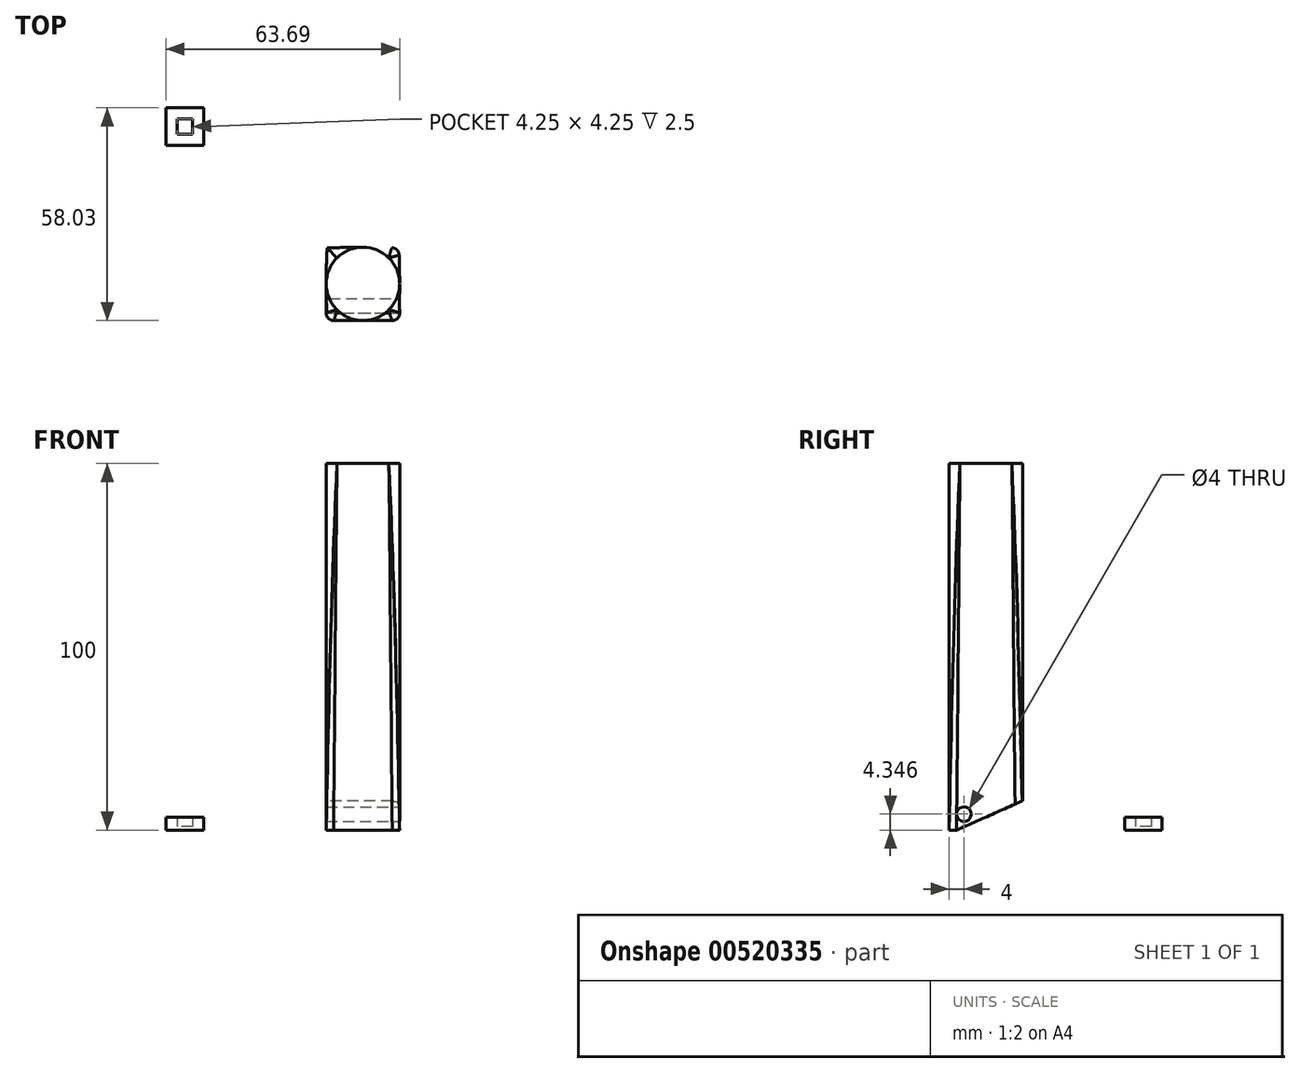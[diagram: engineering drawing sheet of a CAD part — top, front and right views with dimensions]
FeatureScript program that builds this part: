
annotation { "Feature Type Name" : "Feature", "Feature Type Description" : "" }
export const myFeature = defineFeature(function(context is Context, id is Id, definition is map)
    precondition{}
    {
        {
            var Q0;
            Q0=qCreatedBy(makeId("Top.planeOp"),FACE);
            var sketch = newSketch(context, id + "F0", { "sketchPlane" : qUnion([Q0])});
            skLineSegment(sketch, "E0.bottom", {"start": v(10, 10) * mm, "end": v(-10, 10) * mm});
            skLineSegment(sketch, "E0.top", {"start": v(10, -10) * mm, "end": v(-10, -10) * mm});
            skLineSegment(sketch, "E0.left", {"start": v(10, 10) * mm, "end": v(10, -10) * mm});
            skLineSegment(sketch, "E0.right", {"start": v(-10, 10) * mm, "end": v(-10, -10) * mm});
            skPoint(sketch, "E0.middle", {"position": v(0, 0) * mm});
            skSolve(sketch);
        }
        {
            var Q0;
            Q0=qCreatedBy(makeId("Top.planeOp"),FACE);
            cPlane(context, id + "F1", {"entities" : qUnion([Q0]), "cplaneType" : CPlaneType.OFFSET, "offset" : 100 * mm, "width" : 150 * mm, "height" : 150 * mm});
        }
        {
            var Q0;
            Q0=qCreatedBy(id+"F1.planeOp",FACE);
            var sketch = newSketch(context, id + "F2", { "sketchPlane" : qUnion([Q0])});
            skCircle(sketch, "E1", {"center": v(0, 0) * mm, "radius": 10 * mm});
            skSolve(sketch);
        }
        {
            var Q0;
            Q0=makeQuery(id+"F0.imprint","IMPRINT",FACE,{"disambiguationData":[TD([[makeQuery(id+"F0.imprint","IMPRINT",EDGE,{"derivedFrom":sQuery(id+"F0.wireOp",EDGE,"E0.bottom")}),1.0]])]});
            var Q1;
            Q1=makeQuery(id+"F2.imprint","IMPRINT",FACE,{"disambiguationData":[TD([[makeQuery(id+"F2.imprint","IMPRINT",EDGE,{"derivedFrom":sQuery(id+"F2.wireOp",EDGE,"E1")}),1.0]])]});
            loft(context, id + "F3", {"sheetProfilesArray" : [{ "sheetProfileEntities" : qUnion([Q0]) }, { "sheetProfileEntities" : qUnion([Q1]) }]});
        }
        {
            var Q0;
            Q0=qCreatedBy(makeId("Right.planeOp"),FACE);
            cPlane(context, id + "F4", {"entities" : qUnion([Q0]), "cplaneType" : CPlaneType.OFFSET, "offset" : 25 * mm, "width" : 150 * mm, "height" : 150 * mm});
        }
        {
            var Q0;
            Q0=qCreatedBy(id+"F4.planeOp",FACE);
            var sketch = newSketch(context, id + "F5", { "sketchPlane" : qUnion([Q0])});
            skLineSegment(sketch, "E2", {"start": v(-8, 0) * mm, "end": v(10, 8) * mm});
            skLineSegment(sketch, "E3", {"start": v(-8, 0) * mm, "end": v(10, 0) * mm});
            skLineSegment(sketch, "E4", {"start": v(10, 0) * mm, "end": v(10, 8) * mm});
            skCircle(sketch, "E5", {"center": v(-6, 4.35) * mm, "radius": 2 * mm});
            skSolve(sketch);
        }
        {
            var Q0;
            Q0=makeQuery(id+"F5.imprint","IMPRINT",FACE,{"disambiguationData":[TD([[makeQuery(id+"F5.imprint","IMPRINT",EDGE,{"derivedFrom":sQuery(id+"F5.wireOp",EDGE,"E2")}),-1.0]])]});
            var Q1;
            Q1=makeQuery(id+"F5.imprint","IMPRINT",FACE,{"disambiguationData":[TD([[makeQuery(id+"F5.imprint","IMPRINT",EDGE,{"derivedFrom":sQuery(id+"F5.wireOp",EDGE,"E5")}),1.0]])]});
            extrude(context, id + "F6", {"entities" : qUnion([Q0, Q1]), "operationType" : NewBodyOperationType.REMOVE, "endBound" : BoundingType.THROUGH_ALL, "oppositeDirection" : true, "depth" : 25 * mm, "offsetDistance" : 25 * mm});
        }
        {
            var Q0;
            Q0=makeQuery(id+"F3.opLoft","SWEPT_EDGE",EDGE,{"disambiguationData":[OSD([sQuery(id+"F0.wireOp",EDGE,"E0.bottom"),sQuery(id+"F0.wireOp",EDGE,"E0.top"),sQuery(id+"F0.wireOp",EDGE,"E0.right"),sQuery(id+"F2.wireOp",EDGE,"E1")])]});
            var Q1;
            Q1=makeQuery(id+"F3.opLoft","SWEPT_EDGE",EDGE,{"disambiguationData":[OSD([sQuery(id+"F0.wireOp",EDGE,"E0.top"),sQuery(id+"F0.wireOp",EDGE,"E0.left"),sQuery(id+"F0.wireOp",EDGE,"E0.right"),sQuery(id+"F2.wireOp",EDGE,"E1")])]});
            var Q2;
            Q2=makeQuery(id+"F3.opLoft","SWEPT_EDGE",EDGE,{"disambiguationData":[OSD([sQuery(id+"F0.wireOp",EDGE,"E0.bottom"),sQuery(id+"F0.wireOp",EDGE,"E0.left")])]});
            var Q3;
            Q3=makeQuery(id+"F3.opLoft","SWEPT_EDGE",EDGE,{"disambiguationData":[OSD([sQuery(id+"F0.wireOp",EDGE,"E0.bottom"),sQuery(id+"F0.wireOp",EDGE,"E0.left"),sQuery(id+"F0.wireOp",EDGE,"E0.right"),sQuery(id+"F2.wireOp",EDGE,"E1")])]});
            fillet(context, id + "F7", {"entities" : qUnion([Q0, Q1, Q2, Q3]), "radius" : 2 * mm, "tangentPropagation" : true, "allowEdgeOverflow" : false});
        }
        {
            var Q0;
            Q0=qCreatedBy(makeId("Top.planeOp"),FACE);
            var sketch = newSketch(context, id + "F8", { "sketchPlane" : qUnion([Q0])});
            skLineSegment(sketch, "E6.bottom", {"start": v(-46.44, 45.03) * mm, "end": v(-50.7, 45.03) * mm});
            skLineSegment(sketch, "E6.top", {"start": v(-46.44, 40.78) * mm, "end": v(-50.7, 40.78) * mm});
            skLineSegment(sketch, "E6.left", {"start": v(-46.44, 45.03) * mm, "end": v(-46.44, 40.78) * mm});
            skLineSegment(sketch, "E6.right", {"start": v(-50.7, 45.03) * mm, "end": v(-50.7, 40.78) * mm});
            skPoint(sketch, "E6.middle", {"position": v(-48.57, 42.9) * mm});
            skLineSegment(sketch, "E7.0", {"start": v(-43.44, 48.03) * mm, "end": v(-53.7, 48.03) * mm});
            skLineSegment(sketch, "E7.1", {"start": v(-43.44, 48.03) * mm, "end": v(-43.44, 37.78) * mm});
            skLineSegment(sketch, "E7.2", {"start": v(-43.44, 37.78) * mm, "end": v(-53.7, 37.78) * mm});
            skLineSegment(sketch, "E7.3", {"start": v(-53.7, 48.03) * mm, "end": v(-53.7, 37.78) * mm});
            skSolve(sketch);
        }
        {
            var Q0;
            Q0=makeQuery(id+"F8.imprint","IMPRINT",FACE,{"disambiguationData":[TD([[makeQuery(id+"F8.imprint","IMPRINT",EDGE,{"derivedFrom":sQuery(id+"F8.wireOp",EDGE,"E6.bottom")}),1.0]])]});
            extrude(context, id + "F9", {"entities" : qUnion([Q0]), "depth" : 1 * mm, "offsetDistance" : 25 * mm});
        }
        {
            var Q0;
            Q0 = qSketchRegion(id + "F8", true);
            extrude(context, id + "F10", {"entities" : qUnion([Q0]), "operationType" : NewBodyOperationType.ADD, "depth" : 3.5 * mm, "offsetDistance" : 25 * mm});
        }
    });
